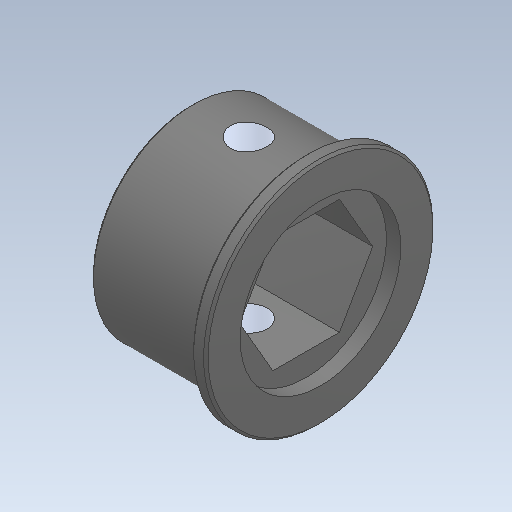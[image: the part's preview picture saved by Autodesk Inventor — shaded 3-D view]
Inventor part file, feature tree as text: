
AUTODESK INVENTOR PART (.ipt)
format: ipt  version: 2020 (Build 240168000, 168)  size: 136,192 bytes
history: native  units: in
note: dims shown in document units (in); Inventor stores cm internally (conversion verified against a paired STEP export)
features: chamfer x1
ambient origin geometry x8: Origin, YZ Plane, XZ Plane, XY Plane, X Axis, Y Axis, Z Axis, Center Point
bodies: Solid1 (feature_tree)
feature tree (1):
  chamfer  "Chamfer1"  [1 undecoded]
note: 1 required parameter value undecoded (feature->parameter linkage not recoverable at this tier; creation-order binding heuristic only, values carry confidence <= 0.55)
